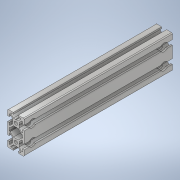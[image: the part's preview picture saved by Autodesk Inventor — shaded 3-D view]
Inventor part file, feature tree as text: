
AUTODESK INVENTOR PART (.ipt)
format: ipt  version: 2022 (Build 260153000, 153)  size: 367,616 bytes
history: native  units: mm
features: other x9, revolve x4, sketch x4, extrude x1, hole x1, pattern_linear x1
ambient origin geometry x8: Origin, YZ Plane, XZ Plane, XY Plane, X Axis, Y Axis, Z Axis, Center Point
bodies: Solid1 (feature_tree)
feature tree (20):
  extrude  "Extrusion1"  Depth=20.0mm TaperAngle=0.0deg
  hole  "Hole1"  [1 undecoded]
  pattern_linear  "Rectangular Pattern1"  Spacing1=360.0deg  [1 undecoded]
  revolve  "Revolution1"  [1 undecoded]
  revolve  "Revolution2"  [1 undecoded]
  revolve  "Revolution3"  [1 undecoded]
  revolve  "Revolution4"  [1 undecoded]
  other  "C1_XY"
  other  "C1_YZ"
  other  "C1_ZX"
  other  "C1_X"
  other  "C1_Y"
  other  "C1_Z"
  other  "C1_Center"
  sketch  "Sketch_1"  dims[d0=180.0mm d1=0.0mm]
  sketch  "Sketch2"  dims[d2=4.2mm d3=6.0mm d4=4.0mm d5=2.0mm d6=90.0deg d7=180.0mm d8=0.0mm d9=20.0mm d11=20.0mm d12=10.0mm d14=0.0mm]
  sketch  "Sketch_50"  dims[d15=360.0deg d16=360.0deg]
  other  "_p_______27_Sketch_50_0"
  sketch  "Sketch_51"  dims[d17=360.0deg d18=360.0deg d19=0.0mm]
  other  "_p_______28_Sketch_51_0"
note: 6 required parameter values undecoded (feature->parameter linkage not recoverable at this tier; creation-order binding heuristic only, values carry confidence <= 0.55)